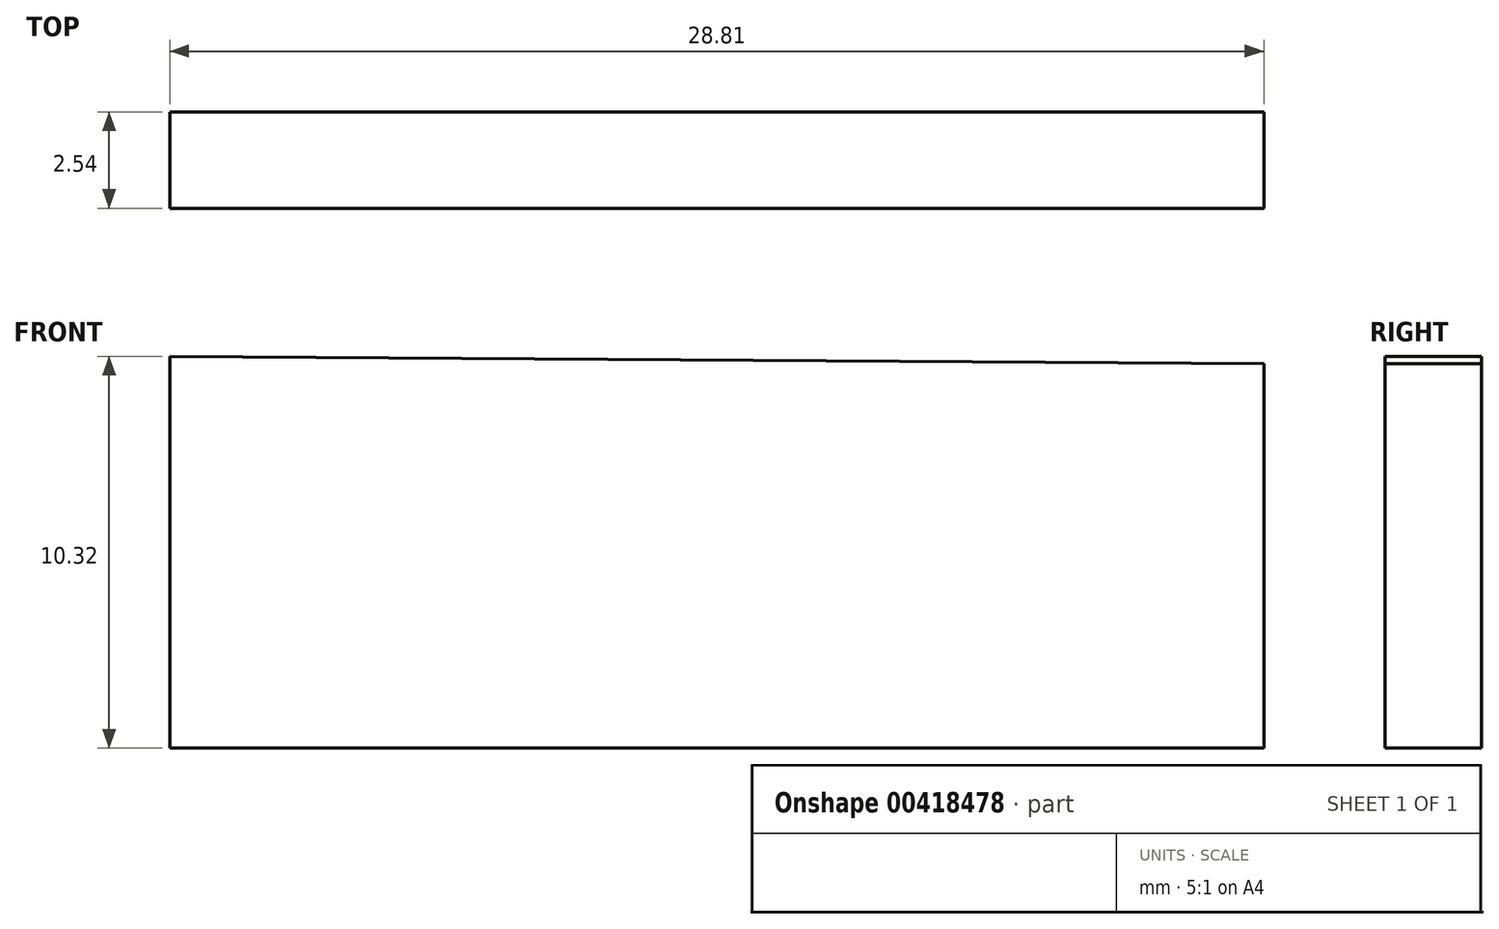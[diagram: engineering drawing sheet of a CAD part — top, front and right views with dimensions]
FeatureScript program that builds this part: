
annotation { "Feature Type Name" : "Feature", "Feature Type Description" : "" }
export const myFeature = defineFeature(function(context is Context, id is Id, definition is map)
    precondition{}
    {
        {
            var Q0;
            Q0=qCreatedBy(makeId("Front.planeOp"),FACE);
            var sketch = newSketch(context, id + "F0", { "sketchPlane" : qUnion([Q0])});
            skLineSegment(sketch, "E0", {"start": v(0, 0) * mm, "end": v(51.2, 0) * mm});
            skLineSegment(sketch, "E1", {"start": v(51.2, 0) * mm, "end": v(48.86, 1.56) * mm});
            skLineSegment(sketch, "E2", {"start": v(48.86, 1.56) * mm, "end": v(0, 1.56) * mm});
            skLineSegment(sketch, "E3", {"start": v(0, 0) * mm, "end": v(0, 4.87) * mm});
            skLineSegment(sketch, "E4", {"start": v(0, 0) * mm, "end": v(0, -5.26) * mm});
            skLineSegment(sketch, "E5", {"start": v(0, -5.26) * mm, "end": v(-28.81, -5.26) * mm});
            skLineSegment(sketch, "E6", {"start": v(-28.81, -5.26) * mm, "end": v(-28.81, 5.06) * mm});
            skLineSegment(sketch, "E7", {"start": v(-28.81, 5.06) * mm, "end": v(0, 4.87) * mm});
            skSolve(sketch);
        }
        {
            var Q0;
            {var subQ0=sQuery(id+"F0.wireOp",EDGE,"E4");Q0=makeQuery(id+"F0.imprint","IMPRINT",FACE,{"disambiguationData":[TD([[makeQuery(id+"F0.imprint","IMPRINT",EDGE,{"derivedFrom":subQ0}),-1.0]])]});}
            extrude(context, id + "F1", {"entities" : qUnion([Q0]), "depth" : 2.54 * mm});
        }
    });
